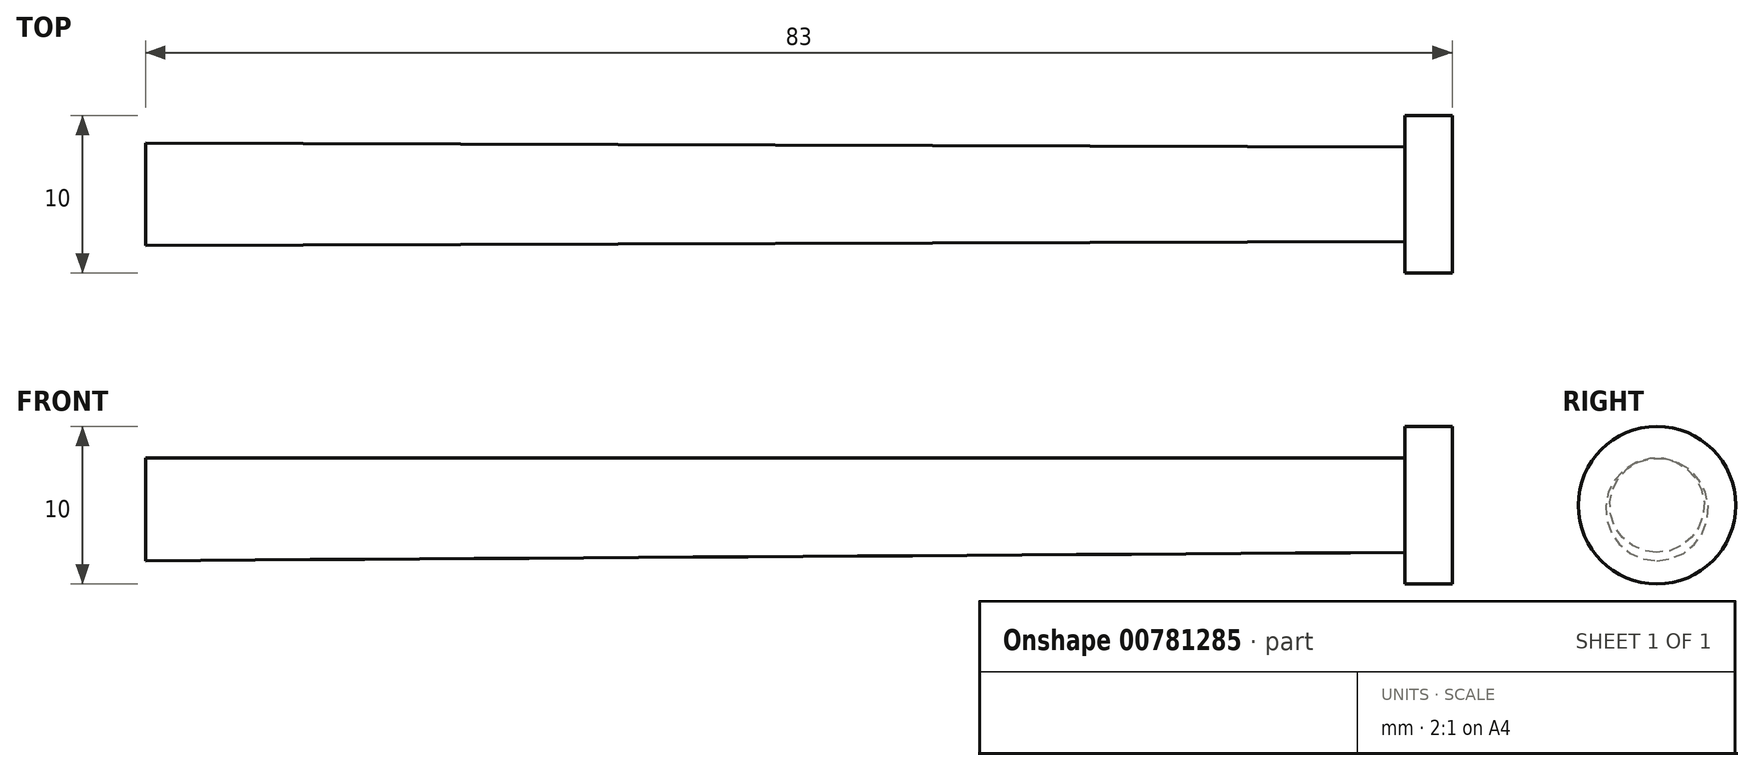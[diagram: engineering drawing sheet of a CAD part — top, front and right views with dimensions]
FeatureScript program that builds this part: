
annotation { "Feature Type Name" : "Feature", "Feature Type Description" : "" }
export const myFeature = defineFeature(function(context is Context, id is Id, definition is map)
    precondition{}
    {
        {
            var Q0;
            Q0=qCreatedBy(makeId("Front.planeOp"),FACE);
            var sketch = newSketch(context, id + "F0", { "sketchPlane" : qUnion([Q0])});
            skLineSegment(sketch, "E0.bottom", {"start": v(1.5, 5) * mm, "end": v(-1.5, 5) * mm});
            skLineSegment(sketch, "E0.top", {"start": v(1.5, -5) * mm, "end": v(-1.5, -5) * mm});
            skLineSegment(sketch, "E0.left", {"start": v(1.5, 5) * mm, "end": v(1.5, -5) * mm});
            skPoint(sketch, "E0.middle", {"position": v(0, 0) * mm});
            skLineSegment(sketch, "E1", {"start": v(-1.5, 5) * mm, "end": v(-1.5, 3) * mm});
            skLineSegment(sketch, "E2", {"start": v(-1.5, -3) * mm, "end": v(-1.5, -5) * mm});
            skLineSegment(sketch, "E3", {"start": v(-1.5, 3) * mm, "end": v(-1.5, -3) * mm});
            skLineSegment(sketch, "E4", {"start": v(-1.5, 3) * mm, "end": v(-81.5, 3) * mm});
            skLineSegment(sketch, "E5", {"start": v(-81.5, 3) * mm, "end": v(-81.5, -3) * mm});
            skLineSegment(sketch, "E6", {"start": v(-81.5, -3) * mm, "end": v(-1.5, -3) * mm});
            skLineSegment(sketch, "E7", {"start": v(1.5, 0) * mm, "end": v(-1.5, 0) * mm});
            skLineSegment(sketch, "E8", {"start": v(-1.5, 0) * mm, "end": v(-81.5, -0.26) * mm});
            skSolve(sketch);
        }
        {
            var Q0;
            {var subQ4=sQuery(id+"F0.wireOp",EDGE,"E0.bottom");Q0=makeQuery(id+"F0.imprint","IMPRINT",FACE,{"disambiguationData":[TD([[makeQuery(id+"F0.imprint","IMPRINT",EDGE,{"derivedFrom":subQ4}),1.0]])]});}
            var Q1;
            Q1=sQuery(id+"F0.wireOp",EDGE,"E7");
            revolve(context, id + "F1", {"surfaceOperationType" : NewSurfaceOperationType.NEW, "entities" : qUnion([Q0]), "axis" : qUnion([Q1]), "revolveType" : RevolveType.FULL});
        }
        {
            var Q0;
            {var subQ0=sQuery(id+"F0.wireOp",EDGE,"E4");Q0=makeQuery(id+"F0.imprint","IMPRINT",FACE,{"disambiguationData":[TD([[makeQuery(id+"F0.imprint","IMPRINT",EDGE,{"derivedFrom":subQ0}),1.0]])]});}
            var Q1;
            Q1=sQuery(id+"F0.wireOp",EDGE,"E8");
            revolve(context, id + "F2", {"operationType" : NewBodyOperationType.ADD, "surfaceOperationType" : NewSurfaceOperationType.NEW, "entities" : qUnion([Q0]), "axis" : qUnion([Q1]), "revolveType" : RevolveType.FULL});
        }
    });
